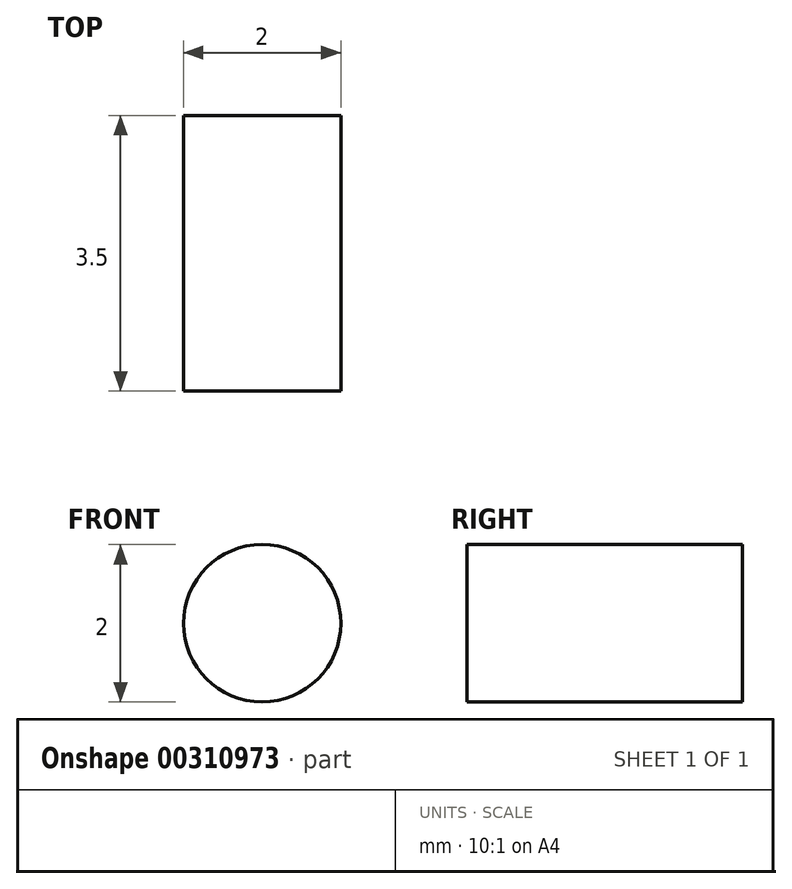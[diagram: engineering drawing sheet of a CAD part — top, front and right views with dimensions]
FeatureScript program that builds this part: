
annotation { "Feature Type Name" : "Feature", "Feature Type Description" : "" }
export const myFeature = defineFeature(function(context is Context, id is Id, definition is map)
    precondition{}
    {
        {
            var Q0;
            Q0=qCreatedBy(makeId("Front.planeOp"),FACE);
            var sketch = newSketch(context, id + "F0", { "sketchPlane" : qUnion([Q0])});
            skCircle(sketch, "E0", {"center": v(0, 0) * mm, "radius": 1 * mm});
            skSolve(sketch);
        }
        {
            var Q0;
            Q0=makeQuery(id+"F0.imprint","IMPRINT",FACE,{"disambiguationData":[TD([[makeQuery(id+"F0.imprint","IMPRINT",EDGE,{"derivedFrom":sQuery(id+"F0.wireOp",EDGE,"E0")}),1.0]])]});
            extrude(context, id + "F1", {"entities" : qUnion([Q0]), "depth" : 3.5 * mm});
        }
    });
